# Revit family: External block S615_3R1A
name_source: partatom
category: Оборудование
units: mm (PartAtom-declared; Revit-internal decimal feet)

## family parameters
Всегда вертикально = Да
Классификация = Нет
На основе рабочей плоскости = Нет
Общий = Нет
При загрузке вырезать с полостями = Нет
Размер круглого соединителя = Использовать диаметр
Тип детали = Нормальный
Точка принадлежности помещению = Нет

## types (1)
- BLHVE-S615-O/3R1A
    00_20_Manufacturer = BLAUBERG
    00_20_Name = External block
    00_20_Type = BLHVE-S615-O/3R1A
    A = 1370 мм
    B = 400 мм
    C = 1740 мм
    Casing Material = Steel, white, mat
    Cp = 635 мм
    Cv = 368 мм
    D = 586 мм
    Dv = 585 мм
    E = 840 мм
    Electric = Нет
    Grid Material = Mesh, steel, painted,  white
    Height = 1740 мм
    Lb = 1340 мм
    Length = 1370 мм
    Load Classification = HVAC
    Lv = 328 мм
    Maintenance zone material = <По категории>
    Maximum Air Flow = 0.0 л/с
    Power = 16800 Вт
    Weight = 297.00 кг
    Width = 400 мм
    d = 16 мм
    d1 = 29 мм
    h = 1720 мм
    rn = 10 мм
    wn = 268 мм
    Изготовитель = BLAUBERG
    Отметка по умолчанию = 0 мм
